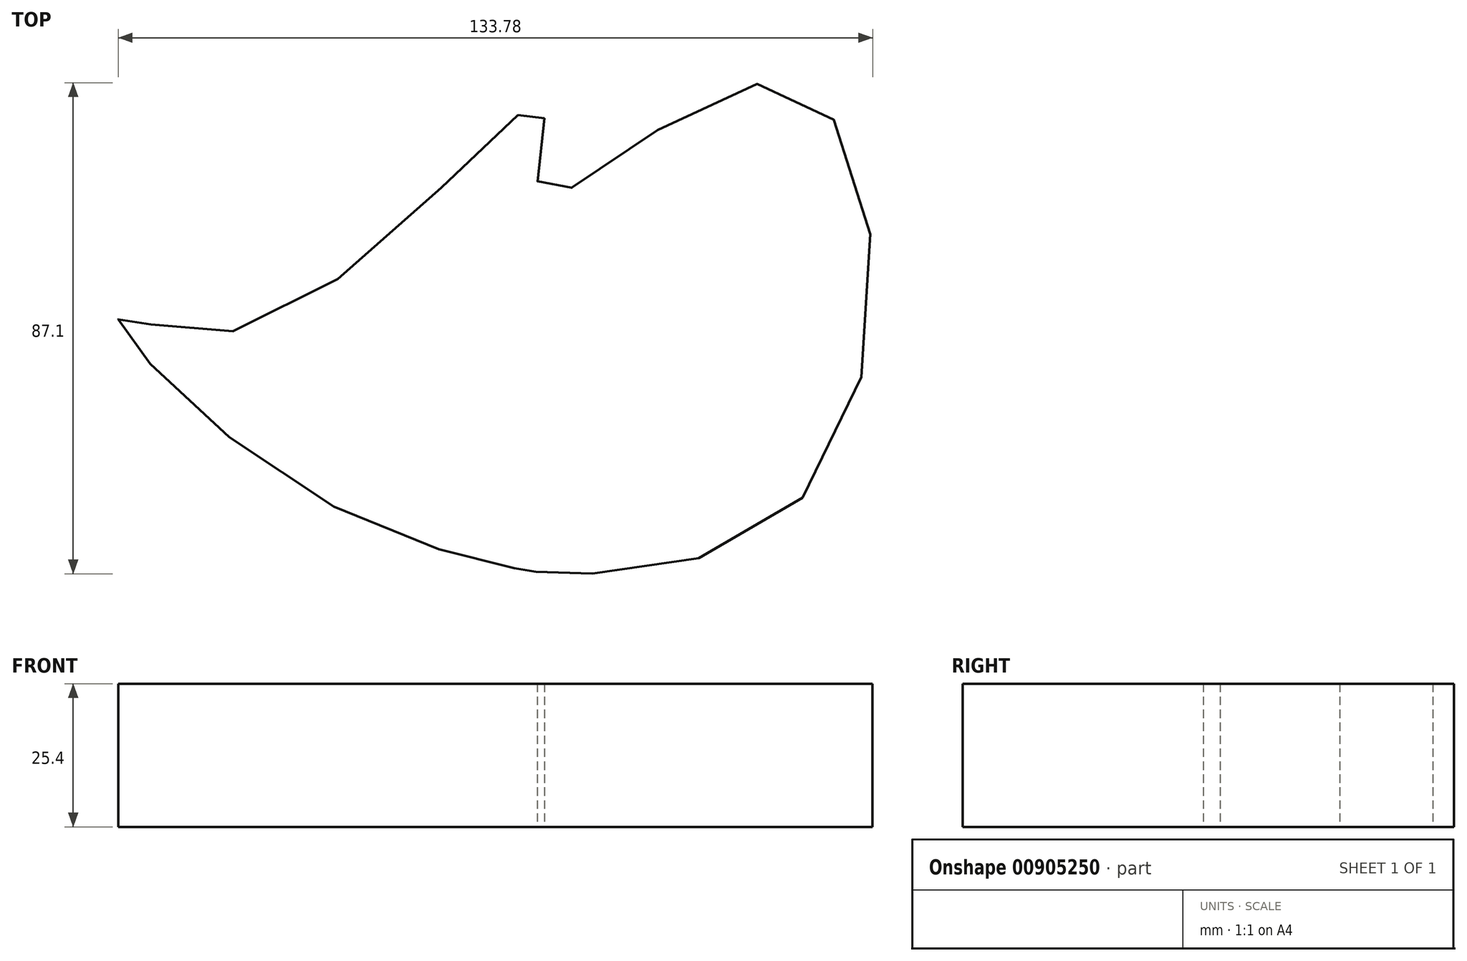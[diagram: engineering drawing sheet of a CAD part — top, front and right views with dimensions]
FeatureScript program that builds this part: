
annotation { "Feature Type Name" : "Feature", "Feature Type Description" : "" }
export const myFeature = defineFeature(function(context is Context, id is Id, definition is map)
    precondition{}
    {
        {
            var Q0;
            Q0=qCreatedBy(makeId("Top.planeOp"),FACE);
            var sketch = newSketch(context, id + "F0", { "sketchPlane" : qUnion([Q0])});
            skFitSpline(sketch, "E0", {"points": [v(46.2, 0) * mm, v(-1.1, -13.13) * mm, v(-1.34, -13.11) * mm, v(-1.57, -13.09) * mm, v(-39.85, 0) * mm, v(-75.09, 31.94) * mm, v(-51, 30.47) * mm, v(0, 69.53) * mm, v(0, 53.67) * mm, v(43.27, 73.35) * mm, v(46.2, 0) * mm]});
            skSolve(sketch);
        }
        {
            var Q0;
            Q0=makeQuery(id+"F0.imprint","IMPRINT",FACE,{"disambiguationData":[TD([[makeQuery(id+"F0.imprint","IMPRINT",EDGE,{"derivedFrom":sQuery(id+"F0.wireOp",EDGE,"E0")}),-1.0]])]});
            extrude(context, id + "F1", {"entities" : qUnion([Q0]), "depth" : 25.4 * mm, "offsetDistance" : 25.4 * mm});
        }
    });
